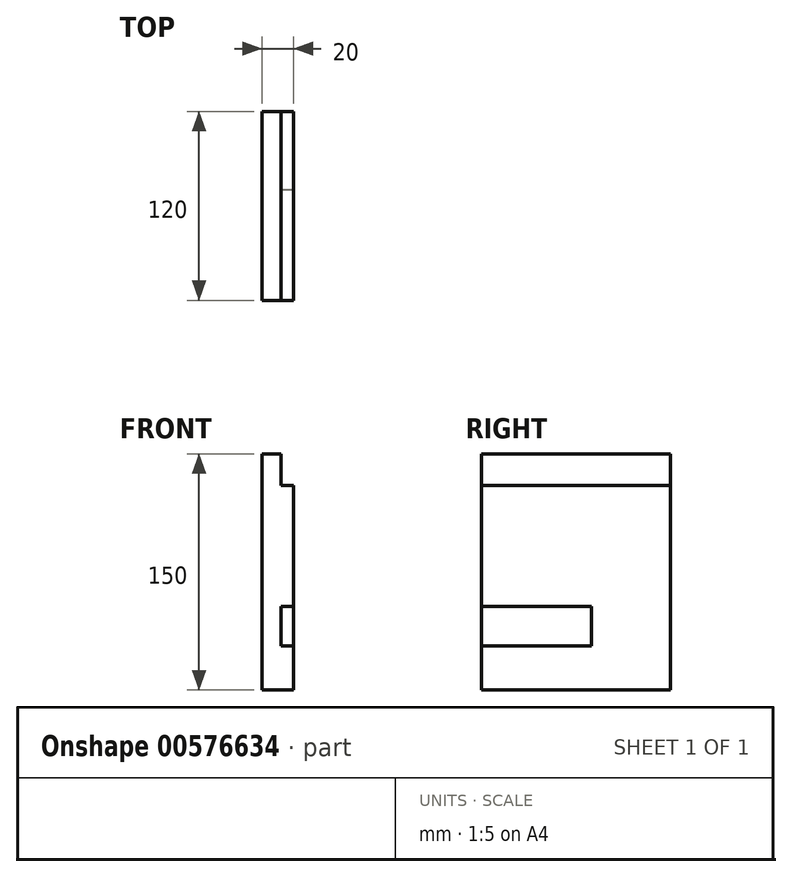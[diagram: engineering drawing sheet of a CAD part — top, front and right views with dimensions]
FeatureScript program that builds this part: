
annotation { "Feature Type Name" : "Feature", "Feature Type Description" : "" }
export const myFeature = defineFeature(function(context is Context, id is Id, definition is map)
    precondition{}
    {
        {
            var Q0;
            Q0=qCreatedBy(makeId("Front.planeOp"),FACE);
            var sketch = newSketch(context, id + "F0", { "sketchPlane" : qUnion([Q0])});
            skLineSegment(sketch, "E0", {"start": v(-76.28, 75) * mm, "end": v(-76.28, -75) * mm});
            skLineSegment(sketch, "E1", {"start": v(-76.28, -75) * mm, "end": v(-56.28, -75) * mm});
            skLineSegment(sketch, "E2", {"start": v(-56.28, -75) * mm, "end": v(-56.28, -47) * mm});
            skLineSegment(sketch, "E3", {"start": v(-56.28, -47) * mm, "end": v(-64.28, -47) * mm});
            skLineSegment(sketch, "E4", {"start": v(-64.28, -47) * mm, "end": v(-64.28, -22) * mm});
            skLineSegment(sketch, "E5", {"start": v(-64.28, -22) * mm, "end": v(-56.28, -22) * mm});
            skLineSegment(sketch, "E6", {"start": v(-56.28, -22) * mm, "end": v(-56.28, 55) * mm});
            skLineSegment(sketch, "E7", {"start": v(-56.28, 55) * mm, "end": v(-64.28, 55) * mm});
            skLineSegment(sketch, "E8", {"start": v(-64.28, 55) * mm, "end": v(-64.28, 75) * mm});
            skLineSegment(sketch, "E9", {"start": v(-64.28, 75) * mm, "end": v(-76.28, 75) * mm});
            skLineSegment(sketch, "E10", {"start": v(-56.28, -47) * mm, "end": v(-56.28, -22) * mm});
            skSolve(sketch);
        }
        {
            var Q0;
            Q0=makeQuery(id+"F0.imprint","IMPRINT",FACE,{"disambiguationData":[TD([[makeQuery(id+"F0.imprint","IMPRINT",EDGE,{"derivedFrom":sQuery(id+"F0.wireOp",EDGE,"E0")}),1.0]])]});
            extrude(context, id + "F1", {"entities" : qUnion([Q0]), "depth" : 120 * mm, "offsetDistance" : 25 * mm});
        }
        {
            var Q0;
            Q0=makeQuery(id+"F0.imprint","IMPRINT",FACE,{"disambiguationData":[TD([[makeQuery(id+"F0.imprint","IMPRINT",EDGE,{"derivedFrom":sQuery(id+"F0.wireOp",EDGE,"E3")}),-1.0]])]});
            extrude(context, id + "F2", {"entities" : qUnion([Q0]), "operationType" : NewBodyOperationType.ADD, "depth" : 50 * mm, "offsetDistance" : 25 * mm});
        }
    });
